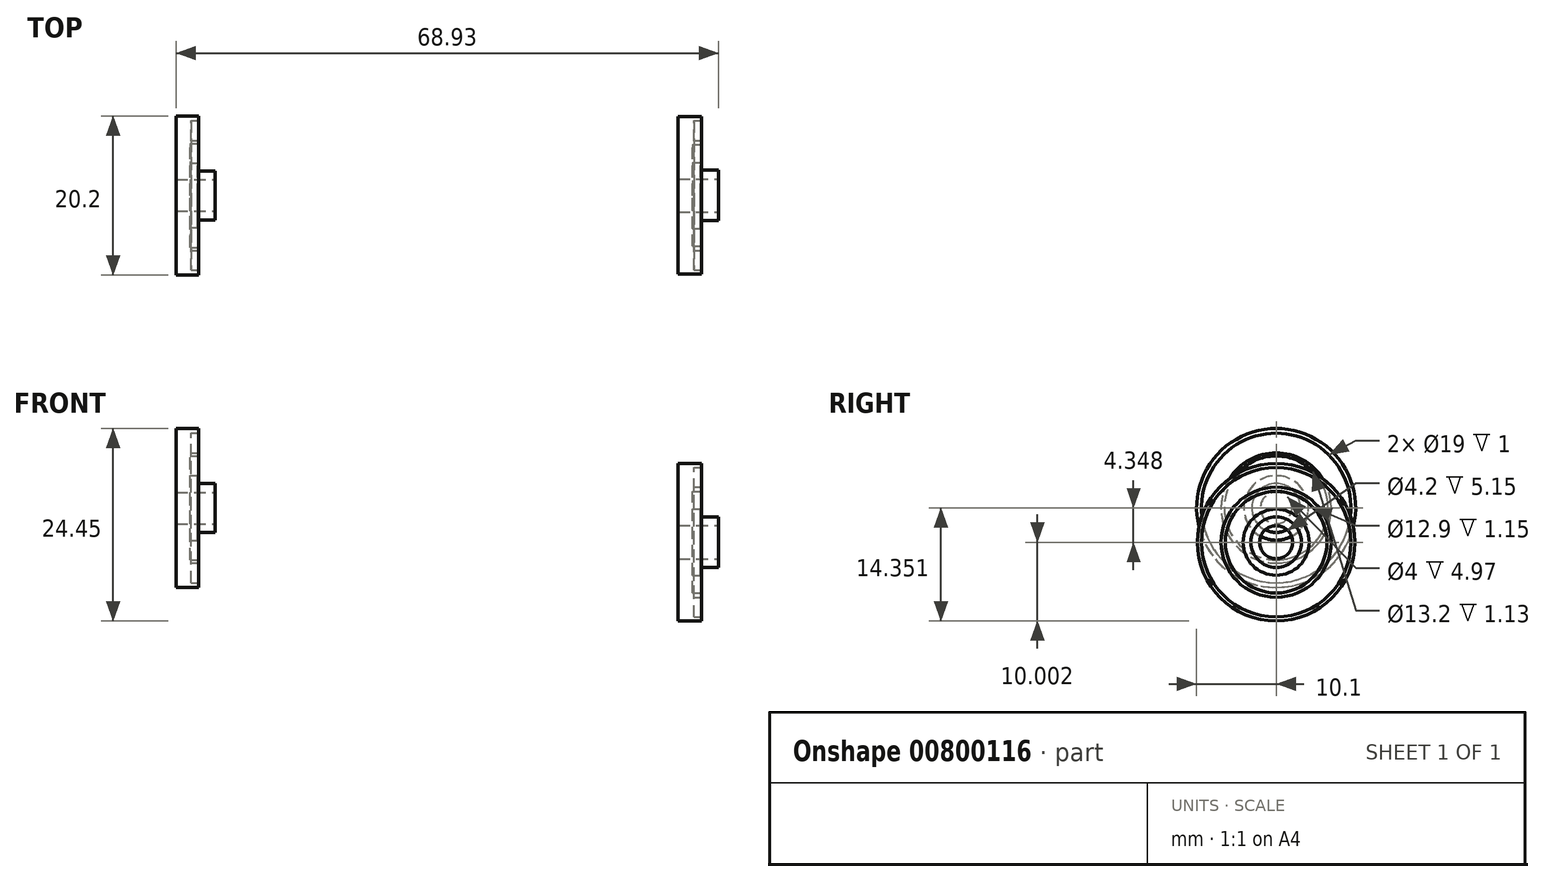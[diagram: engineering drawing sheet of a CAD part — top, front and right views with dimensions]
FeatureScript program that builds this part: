
annotation { "Feature Type Name" : "Feature", "Feature Type Description" : "" }
export const myFeature = defineFeature(function(context is Context, id is Id, definition is map)
    precondition{}
    {
        {
            var Q0;
            Q0=qCreatedBy(makeId("Front.planeOp"),FACE);
            var sketch = newSketch(context, id + "F0", { "sketchPlane" : qUnion([Q0])});
            skLineSegment(sketch, "E0", {"start": v(0, 0) * mm, "end": v(0, 25) * mm});
            skLineSegment(sketch, "E1", {"start": v(0, 25) * mm, "end": v(4, 25) * mm});
            skLineSegment(sketch, "E2", {"start": v(4, 0) * mm, "end": v(0, 0) * mm});
            skLineSegment(sketch, "E3", {"start": v(4, 0) * mm, "end": v(16.3, 0) * mm});
            skLineSegment(sketch, "E4", {"start": v(16.3, 0) * mm, "end": v(16.3, 2) * mm});
            skLineSegment(sketch, "E5", {"start": v(16.3, 2) * mm, "end": v(16.3, 2.98) * mm});
            skLineSegment(sketch, "E6", {"start": v(16.3, 2.98) * mm, "end": v(14, 2.98) * mm});
            skLineSegment(sketch, "E7", {"start": v(14, 2.98) * mm, "end": v(14, 4.48) * mm});
            skLineSegment(sketch, "E8", {"start": v(14, 4.48) * mm, "end": v(13, 4.48) * mm});
            skLineSegment(sketch, "E9", {"start": v(13, 4.48) * mm, "end": v(13, 6.6) * mm});
            skLineSegment(sketch, "E10", {"start": v(13, 6.6) * mm, "end": v(14.13, 6.6) * mm});
            skLineSegment(sketch, "E11", {"start": v(14.13, 6.6) * mm, "end": v(14.13, 7) * mm});
            skLineSegment(sketch, "E12", {"start": v(14.13, 7) * mm, "end": v(13.13, 7) * mm});
            skLineSegment(sketch, "E13", {"start": v(13.13, 7) * mm, "end": v(13.13, 9.7) * mm});
            skLineSegment(sketch, "E14", {"start": v(13.13, 9.7) * mm, "end": v(14.13, 9.7) * mm});
            skFitSpline(sketch, "E15", {"points": [v(4, 25) * mm, v(7.93, 22.38) * mm, v(11.47, 13.84) * mm, v(14.06, 9.93) * mm, v(14.13, 9.7) * mm], "startDerivative": vector(13.17, -0.72) * mm, "endDerivative": vector(0.18, -4.68) * mm});
            skLineSegment(sketch, "E16", {"start": v(4, 25) * mm, "end": v(4, 21) * mm});
            skLineSegment(sketch, "E17", {"start": v(4, 21) * mm, "end": v(7.4, 21) * mm});
            skLineSegment(sketch, "E18", {"start": v(7.4, 21) * mm, "end": v(7.4, 14.6) * mm});
            skLineSegment(sketch, "E19", {"start": v(7.4, 14.6) * mm, "end": v(4, 14.6) * mm});
            skPoint(sketch, "E20.startSnap0", {"position": v(15.15, 2.98) * mm});
            skLineSegment(sketch, "E21", {"start": v(11.47, 2.98) * mm, "end": v(11.47, 2) * mm});
            skLineSegment(sketch, "E22", {"start": v(11.47, 2) * mm, "end": v(16.3, 2) * mm});
            skLineSegment(sketch, "E23", {"start": v(11.47, 2.98) * mm, "end": v(8.47, 2.98) * mm});
            skLineSegment(sketch, "E24", {"start": v(4, 14.6) * mm, "end": v(4, 13) * mm});
            skLineSegment(sketch, "E25", {"start": v(4, 13) * mm, "end": v(8.47, 13) * mm});
            skLineSegment(sketch, "E26", {"start": v(8.47, 13) * mm, "end": v(8.47, 2.98) * mm});
            skLineSegment(sketch, "E27", {"start": v(4, 25) * mm, "end": v(4, 0) * mm});
            skPoint(sketch, "E28", {"position": v(8.47, 0) * mm});
            skSolve(sketch);
        }
        {
            var Q0;
            Q0=qCreatedBy(makeId("Front.planeOp"),FACE);
            var sketch = newSketch(context, id + "F1", { "sketchPlane" : qUnion([Q0])});
            skPoint(sketch, "E29", {"position": v(36.58, 0) * mm});
            skLineSegment(sketch, "E30", {"start": v(39.5, -3.07) * mm, "end": v(39.5, -1.97) * mm});
            skLineSegment(sketch, "E31", {"start": v(39.5, -1.97) * mm, "end": v(37.25, -1.97) * mm});
            skLineSegment(sketch, "E32", {"start": v(37.25, -1.97) * mm, "end": v(37.25, -0.97) * mm});
            skLineSegment(sketch, "E33", {"start": v(37.25, -0.97) * mm, "end": v(36.3, -0.97) * mm});
            skLineSegment(sketch, "E34", {"start": v(36.3, -0.97) * mm, "end": v(36.3, 1.53) * mm});
            skLineSegment(sketch, "E35", {"start": v(36.3, 1.53) * mm, "end": v(37.43, 1.53) * mm});
            skLineSegment(sketch, "E36", {"start": v(37.43, 1.53) * mm, "end": v(37.43, 1.93) * mm});
            skLineSegment(sketch, "E37", {"start": v(37.43, 1.93) * mm, "end": v(36.43, 1.93) * mm});
            skLineSegment(sketch, "E38", {"start": v(36.43, 1.93) * mm, "end": v(36.43, 4.43) * mm});
            skLineSegment(sketch, "E39", {"start": v(36.43, 4.43) * mm, "end": v(37.43, 4.43) * mm});
            skPoint(sketch, "E40.startSnap0", {"position": v(38.37, -1.97) * mm});
            skLineSegment(sketch, "E41", {"start": v(37.43, 4.43) * mm, "end": v(37.43, 5.03) * mm});
            skLineSegment(sketch, "E42", {"start": v(37.43, 5.03) * mm, "end": v(34.53, 5.03) * mm});
            skLineSegment(sketch, "E43", {"start": v(34.53, 5.03) * mm, "end": v(34.53, -3.07) * mm});
            skLineSegment(sketch, "E44", {"start": v(34.53, -3.07) * mm, "end": v(39.5, -3.07) * mm});
            skLineSegment(sketch, "E45", {"start": v(39.5, -5.07) * mm, "end": v(38.22, -5.07) * mm});
            skSolve(sketch);
        }
        {
            var Q0;
            Q0=qCreatedBy(makeId("Front.planeOp"),FACE);
            var sketch = newSketch(context, id + "F2", { "sketchPlane" : qUnion([Q0])});
            skPoint(sketch, "E46", {"position": v(65.17, -1.26) * mm});
            skLineSegment(sketch, "E47", {"start": v(68.22, -4.33) * mm, "end": v(68.22, -3.23) * mm});
            skLineSegment(sketch, "E48", {"start": v(68.22, -3.23) * mm, "end": v(65.97, -3.23) * mm});
            skLineSegment(sketch, "E49", {"start": v(65.97, -3.23) * mm, "end": v(65.97, -2.23) * mm});
            skLineSegment(sketch, "E50", {"start": v(65.97, -2.23) * mm, "end": v(65.02, -2.23) * mm});
            skLineSegment(sketch, "E51", {"start": v(65.02, -2.23) * mm, "end": v(65.02, 0.27) * mm});
            skLineSegment(sketch, "E52", {"start": v(65.02, 0.27) * mm, "end": v(66.15, 0.27) * mm});
            skLineSegment(sketch, "E53", {"start": v(66.15, 0.27) * mm, "end": v(66.15, 0.97) * mm});
            skPoint(sketch, "E54.startSnap0", {"position": v(67.1, -3.23) * mm});
            skLineSegment(sketch, "E55", {"start": v(63.95, -4.33) * mm, "end": v(68.22, -4.33) * mm});
            skLineSegment(sketch, "E56", {"start": v(68.22, -6.33) * mm, "end": v(66.9, -6.33) * mm});
            skLineSegment(sketch, "E57", {"start": v(63.95, 0.97) * mm, "end": v(63.95, -4.33) * mm});
            skPoint(sketch, "E58.orphan", {"position": v(63.05, -4.33) * mm});
            skLineSegment(sketch, "E59", {"start": v(66.15, 0.97) * mm, "end": v(63.95, 0.97) * mm});
            skSolve(sketch);
        }
        {
            var Q0;
            Q0=makeQuery(id+"F1.imprint","IMPRINT",FACE,{"disambiguationData":[TD([[makeQuery(id+"F1.imprint","IMPRINT",EDGE,{"derivedFrom":sQuery(id+"F1.wireOp",EDGE,"E30")}),1.0]])]});
            var Q1;
            Q1=sQuery(id+"F1.wireOp",EDGE,"E45");
            revolve(context, id + "F3", {"entities" : qUnion([Q0]), "axis" : qUnion([Q1]), "revolveType" : RevolveType.FULL});
        }
        {
            var Q0;
            Q0=qCreatedBy(makeId("Front.planeOp"),FACE);
            var sketch = newSketch(context, id + "F4", { "sketchPlane" : qUnion([Q0])});
            skPoint(sketch, "E60", {"position": v(100.34, -4.5) * mm});
            skLineSegment(sketch, "E61", {"start": v(103.46, -7.32) * mm, "end": v(103.46, -6.22) * mm});
            skLineSegment(sketch, "E62", {"start": v(103.46, -6.22) * mm, "end": v(101.16, -6.22) * mm});
            skLineSegment(sketch, "E63", {"start": v(101.16, -6.22) * mm, "end": v(101.16, -5.22) * mm});
            skLineSegment(sketch, "E64", {"start": v(101.16, -5.22) * mm, "end": v(100.16, -5.22) * mm});
            skLineSegment(sketch, "E65", {"start": v(100.16, -5.22) * mm, "end": v(100.16, -2.97) * mm});
            skLineSegment(sketch, "E66", {"start": v(100.16, -2.97) * mm, "end": v(101.3, -2.97) * mm});
            skLineSegment(sketch, "E67", {"start": v(101.3, -2.97) * mm, "end": v(101.3, -2.42) * mm});
            skLineSegment(sketch, "E68", {"start": v(101.3, -2.42) * mm, "end": v(100.3, -2.42) * mm});
            skLineSegment(sketch, "E69", {"start": v(100.3, -2.42) * mm, "end": v(100.3, 0.08) * mm});
            skLineSegment(sketch, "E70", {"start": v(100.3, 0.08) * mm, "end": v(101.3, 0.08) * mm});
            skPoint(sketch, "E71.startSnap0", {"position": v(102.3, -6.22) * mm});
            skLineSegment(sketch, "E72", {"start": v(101.3, 0.08) * mm, "end": v(101.3, 0.58) * mm});
            skLineSegment(sketch, "E73", {"start": v(101.3, 0.58) * mm, "end": v(98.3, 0.58) * mm});
            skLineSegment(sketch, "E74", {"start": v(98.3, 0.58) * mm, "end": v(98.3, -7.32) * mm});
            skLineSegment(sketch, "E75", {"start": v(98.3, -7.32) * mm, "end": v(103.46, -7.32) * mm});
            skLineSegment(sketch, "E76", {"start": v(103.46, -9.42) * mm, "end": v(102.18, -9.42) * mm});
            skSolve(sketch);
        }
        {
            var Q0;
            Q0=makeQuery(id+"F4.imprint","IMPRINT",FACE,{"disambiguationData":[TD([[makeQuery(id+"F4.imprint","IMPRINT",EDGE,{"derivedFrom":sQuery(id+"F4.wireOp",EDGE,"E61")}),1.0]])]});
            var Q1;
            Q1=sQuery(id+"F4.wireOp",EDGE,"E76");
            revolve(context, id + "F5", {"entities" : qUnion([Q0]), "axis" : qUnion([Q1]), "revolveType" : RevolveType.FULL});
        }
    });
